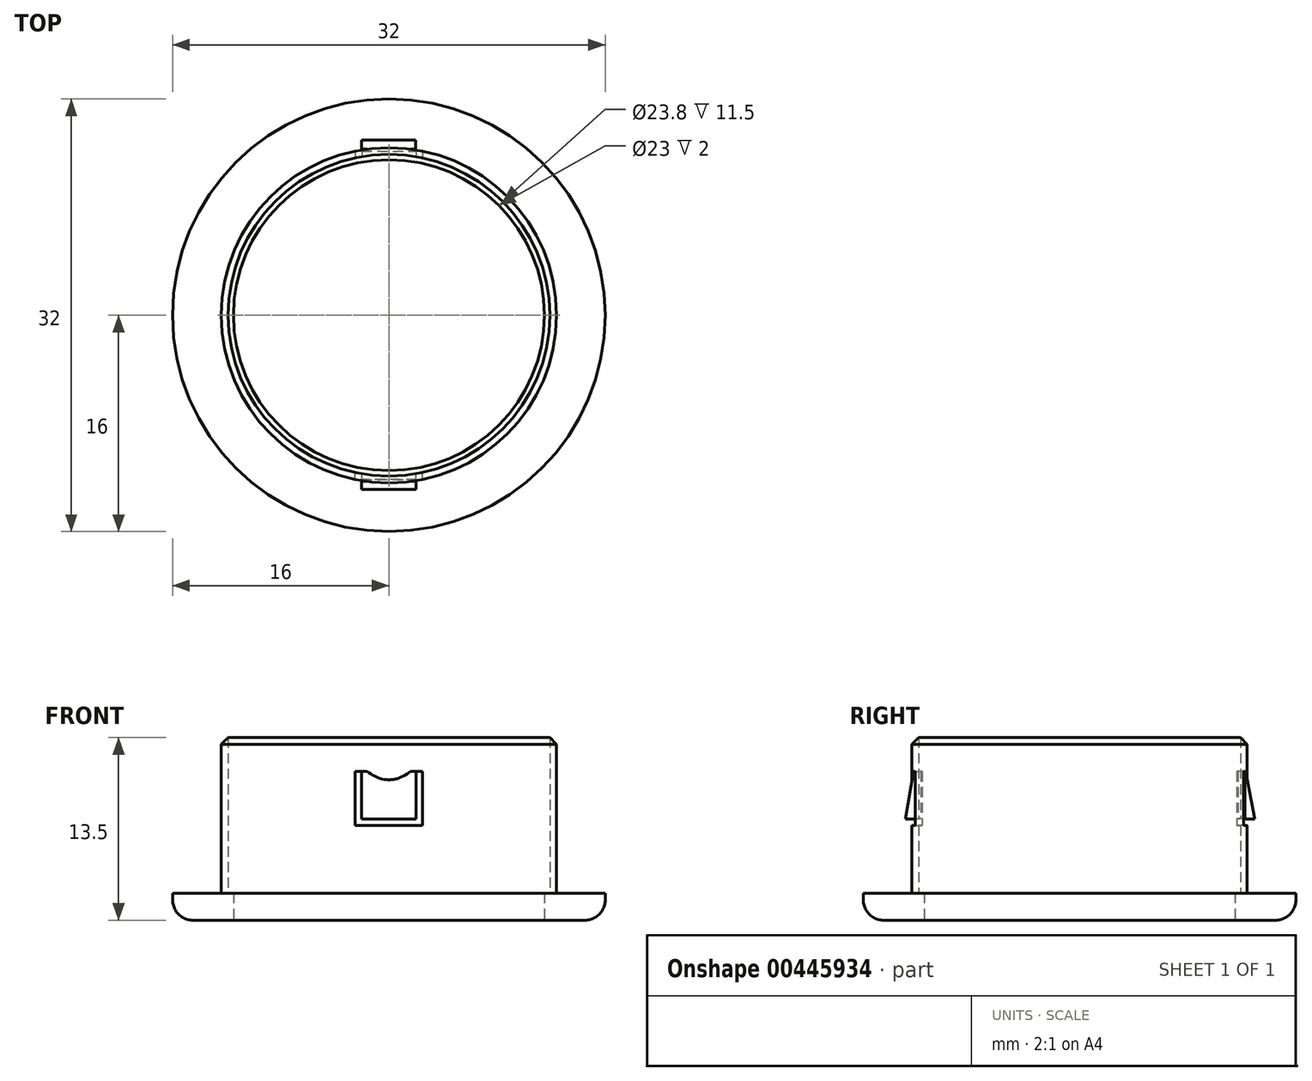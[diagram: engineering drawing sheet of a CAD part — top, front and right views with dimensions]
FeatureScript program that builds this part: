
annotation { "Feature Type Name" : "Feature", "Feature Type Description" : "" }
export const myFeature = defineFeature(function(context is Context, id is Id, definition is map)
    precondition{}
    {
        {
            var Q0;
            Q0=qCreatedBy(makeId("Top.planeOp"),FACE);
            var sketch = newSketch(context, id + "F0", { "sketchPlane" : qUnion([Q0])});
            skCircle(sketch, "E0", {"center": v(0, 0) * mm, "radius": 16 * mm});
            skCircle(sketch, "E1", {"center": v(0, 0) * mm, "radius": 11.5 * mm});
            skSolve(sketch);
        }
        {
            var Q0;
            Q0 = qSketchRegion(id + "F0", true);
            extrude(context, id + "F1", {"entities" : qUnion([Q0]), "depth" : 2 * mm});
        }
        {
            var Q0;
            Q0=makeQuery(id+"F1.opExtrude","CAP_FACE",FACE,{"disambiguationData":[OSD([sQuery(id+"F0.wireOp",EDGE,"E0"),sQuery(id+"F0.wireOp",EDGE,"E1")])],"isStart":false});
            var sketch = newSketch(context, id + "F2", { "sketchPlane" : qUnion([Q0])});
            skCircle(sketch, "E2", {"center": v(0, 0) * mm, "radius": 11.9 * mm});
            skCircle(sketch, "E3", {"center": v(0, 0) * mm, "radius": 12.4 * mm});
            skSolve(sketch);
        }
        {
            var Q0;
            Q0 = qSketchRegion(id + "F2", true);
            extrude(context, id + "F3", {"entities" : qUnion([Q0]), "operationType" : NewBodyOperationType.ADD, "depth" : 12 * mm});
        }
        {
            var Q0;
            Q0=qCreatedBy(makeId("Front.planeOp"),FACE);
            var sketch = newSketch(context, id + "F4", { "sketchPlane" : qUnion([Q0])});
            skLineSegment(sketch, "E4", {"start": v(-2.5, 11) * mm, "end": v(-2.5, 7) * mm});
            skLineSegment(sketch, "E5", {"start": v(-2.5, 7) * mm, "end": v(2.5, 7) * mm});
            skLineSegment(sketch, "E6", {"start": v(2.5, 7) * mm, "end": v(2.5, 11) * mm});
            skLineSegment(sketch, "E7", {"start": v(-2, 11) * mm, "end": v(-2, 7.5) * mm});
            skLineSegment(sketch, "E8", {"start": v(-2, 7.5) * mm, "end": v(2, 7.5) * mm});
            skLineSegment(sketch, "E9", {"start": v(2, 7.5) * mm, "end": v(2, 11) * mm});
            skLineSegment(sketch, "E10", {"start": v(-2.5, 11) * mm, "end": v(-2, 11) * mm});
            skLineSegment(sketch, "E11", {"start": v(2, 11) * mm, "end": v(2.5, 11) * mm});
            skSolve(sketch);
        }
        {
            var Q0;
            Q0 = qSketchRegion(id + "F4", true);
            extrude(context, id + "F5", {"entities" : qUnion([Q0]), "operationType" : NewBodyOperationType.REMOVE, "oppositeDirection" : true, "depth" : 25 * mm});
        }
        {
            var Q0;
            Q0 = qSketchRegion(id + "F4", true);
            extrude(context, id + "F6", {"entities" : qUnion([Q0]), "operationType" : NewBodyOperationType.REMOVE, "depth" : 25 * mm});
        }
        {
            var Q0;
            Q0=makeQuery(id+"F5.boolean.opBoolean","INTERSECT",VERTEX,{"derivedFrom":[makeQuery(id+"F3.opExtrude","SWEPT_FACE",FACE,{"disambiguationData":[OSD([sQuery(id+"F2.wireOp",EDGE,"E3")])]}),makeQuery(id+"F5.opExtrude","SWEPT_FACE",FACE,{"disambiguationData":[OSD([sQuery(id+"F4.wireOp",EDGE,"E4")])]}),makeQuery(id+"F5.opExtrude","SWEPT_FACE",FACE,{"disambiguationData":[OSD([sQuery(id+"F4.wireOp",EDGE,"E10")])]})]});
            var Q1;
            Q1=makeQuery(id+"F5.boolean.opBoolean","INTERSECT",VERTEX,{"derivedFrom":[makeQuery(id+"F3.opExtrude","SWEPT_FACE",FACE,{"disambiguationData":[OSD([sQuery(id+"F2.wireOp",EDGE,"E3")])]}),makeQuery(id+"F5.opExtrude","SWEPT_FACE",FACE,{"disambiguationData":[OSD([sQuery(id+"F4.wireOp",EDGE,"E4")])]}),makeQuery(id+"F5.opExtrude","SWEPT_FACE",FACE,{"disambiguationData":[OSD([sQuery(id+"F4.wireOp",EDGE,"E5")])]})]});
            var Q2;
            Q2=makeQuery(id+"F5.boolean.opBoolean","INTERSECT",VERTEX,{"derivedFrom":[makeQuery(id+"F3.opExtrude","SWEPT_FACE",FACE,{"disambiguationData":[OSD([sQuery(id+"F2.wireOp",EDGE,"E3")])]}),makeQuery(id+"F5.opExtrude","SWEPT_FACE",FACE,{"disambiguationData":[OSD([sQuery(id+"F4.wireOp",EDGE,"E6")])]}),makeQuery(id+"F5.opExtrude","SWEPT_FACE",FACE,{"disambiguationData":[OSD([sQuery(id+"F4.wireOp",EDGE,"E11")])]})]});
            cPlane(context, id + "F7", {"entities" : qUnion([Q0, Q1, Q2]), "cplaneType" : CPlaneType.THREE_POINT, "offset" : 25 * mm, "width" : 150 * mm, "height" : 150 * mm});
        }
        {
            var Q0;
            Q0=qCreatedBy(id+"F7.planeOp",FACE);
            var sketch = newSketch(context, id + "F8", { "sketchPlane" : qUnion([Q0])});
            skLineSegment(sketch, "E12.bottom", {"start": v(2.01, 7.49) * mm, "end": v(-1.98, 7.49) * mm});
            skLineSegment(sketch, "E12.top", {"start": v(2.01, 10.98) * mm, "end": v(-1.98, 10.98) * mm});
            skLineSegment(sketch, "E12.left", {"start": v(2.01, 7.49) * mm, "end": v(2.01, 10.98) * mm});
            skLineSegment(sketch, "E12.right", {"start": v(-1.98, 7.49) * mm, "end": v(-1.98, 10.98) * mm});
            skSolve(sketch);
        }
        {
            var Q0;
            Q0 = qSketchRegion(id + "F8", true);
            extrude(context, id + "F9", {"entities" : qUnion([Q0]), "operationType" : NewBodyOperationType.ADD, "depth" : 1 * mm});
        }
        {
            var Q0;
            Q0=makeQuery(id+"F9.opExtrude","CAP_EDGE",EDGE,{"disambiguationData":[OSD([sQuery(id+"F8.wireOp",EDGE,"E12.top")])],"isStart":false});
            chamfer(context, id + "F10", {"entities" : qUnion([Q0]), "chamferType" : ChamferType.TWO_OFFSETS, "width1" : .85 * mm, "oppositeDirection" : true, "width2" : 4.5 * mm, "tangentPropagation" : true});
        }
        {
            var Q0;
            Q0=makeQuery(id+"F6.boolean.opBoolean","INTERSECT",VERTEX,{"derivedFrom":[makeQuery(id+"F3.opExtrude","SWEPT_FACE",FACE,{"disambiguationData":[OSD([sQuery(id+"F2.wireOp",EDGE,"E3")])]}),makeQuery(id+"F6.opExtrude","SWEPT_FACE",FACE,{"disambiguationData":[OSD([sQuery(id+"F4.wireOp",EDGE,"E6")])]}),makeQuery(id+"F6.opExtrude","SWEPT_FACE",FACE,{"disambiguationData":[OSD([sQuery(id+"F4.wireOp",EDGE,"E11")])]})]});
            var Q1;
            Q1=makeQuery(id+"F6.boolean.opBoolean","INTERSECT",VERTEX,{"derivedFrom":[makeQuery(id+"F3.opExtrude","SWEPT_FACE",FACE,{"disambiguationData":[OSD([sQuery(id+"F2.wireOp",EDGE,"E3")])]}),makeQuery(id+"F6.opExtrude","SWEPT_FACE",FACE,{"disambiguationData":[OSD([sQuery(id+"F4.wireOp",EDGE,"E5")])]}),makeQuery(id+"F6.opExtrude","SWEPT_FACE",FACE,{"disambiguationData":[OSD([sQuery(id+"F4.wireOp",EDGE,"E6")])]})]});
            var Q2;
            Q2=makeQuery(id+"F6.boolean.opBoolean","INTERSECT",VERTEX,{"derivedFrom":[makeQuery(id+"F3.opExtrude","SWEPT_FACE",FACE,{"disambiguationData":[OSD([sQuery(id+"F2.wireOp",EDGE,"E3")])]}),makeQuery(id+"F6.opExtrude","SWEPT_FACE",FACE,{"disambiguationData":[OSD([sQuery(id+"F4.wireOp",EDGE,"E4")])]}),makeQuery(id+"F6.opExtrude","SWEPT_FACE",FACE,{"disambiguationData":[OSD([sQuery(id+"F4.wireOp",EDGE,"E5")])]})]});
            cPlane(context, id + "F11", {"entities" : qUnion([Q0, Q1, Q2]), "cplaneType" : CPlaneType.THREE_POINT, "offset" : 25 * mm, "width" : 150 * mm, "height" : 150 * mm});
        }
        {
            var Q0;
            Q0=qCreatedBy(id+"F11.planeOp",FACE);
            var sketch = newSketch(context, id + "F12", { "sketchPlane" : qUnion([Q0])});
            skLineSegment(sketch, "E13.bottom", {"start": v(2.02, 7.49) * mm, "end": v(-2.02, 7.49) * mm});
            skLineSegment(sketch, "E13.top", {"start": v(2.02, 11) * mm, "end": v(-2.02, 11) * mm});
            skLineSegment(sketch, "E13.left", {"start": v(2.02, 7.49) * mm, "end": v(2.02, 11) * mm});
            skLineSegment(sketch, "E13.right", {"start": v(-2.02, 7.49) * mm, "end": v(-2.02, 11) * mm});
            skSolve(sketch);
        }
        {
            var Q0;
            Q0 = qSketchRegion(id + "F12", true);
            extrude(context, id + "F13", {"entities" : qUnion([Q0]), "operationType" : NewBodyOperationType.ADD, "depth" : 1 * mm});
        }
        {
            var Q0;
            Q0=makeQuery(id+"F13.opExtrude","CAP_EDGE",EDGE,{"disambiguationData":[OSD([sQuery(id+"F12.wireOp",EDGE,"E13.top")])],"isStart":false});
            chamfer(context, id + "F14", {"entities" : qUnion([Q0]), "chamferType" : ChamferType.TWO_OFFSETS, "width1" : .85 * mm, "oppositeDirection" : true, "width2" : 5 * mm, "tangentPropagation" : true});
        }
        {
            var Q0;
            Q0=makeQuery(id+"F3.opExtrude","CAP_EDGE",EDGE,{"disambiguationData":[OSD([sQuery(id+"F2.wireOp",EDGE,"E3")])],"isStart":false});
            chamfer(context, id + "F15", {"entities" : qUnion([Q0]), "width" : 1 * mm, "tangentPropagation" : true});
        }
        {
            var Q0;
            Q0=makeQuery(id+"F1.opExtrude","CAP_EDGE",EDGE,{"disambiguationData":[OSD([sQuery(id+"F0.wireOp",EDGE,"E0")])],"isStart":true});
            fillet(context, id + "F16", {"entities" : qUnion([Q0]), "radius" : 1.5 * mm, "tangentPropagation" : true, "allowEdgeOverflow" : false});
        }
    });
